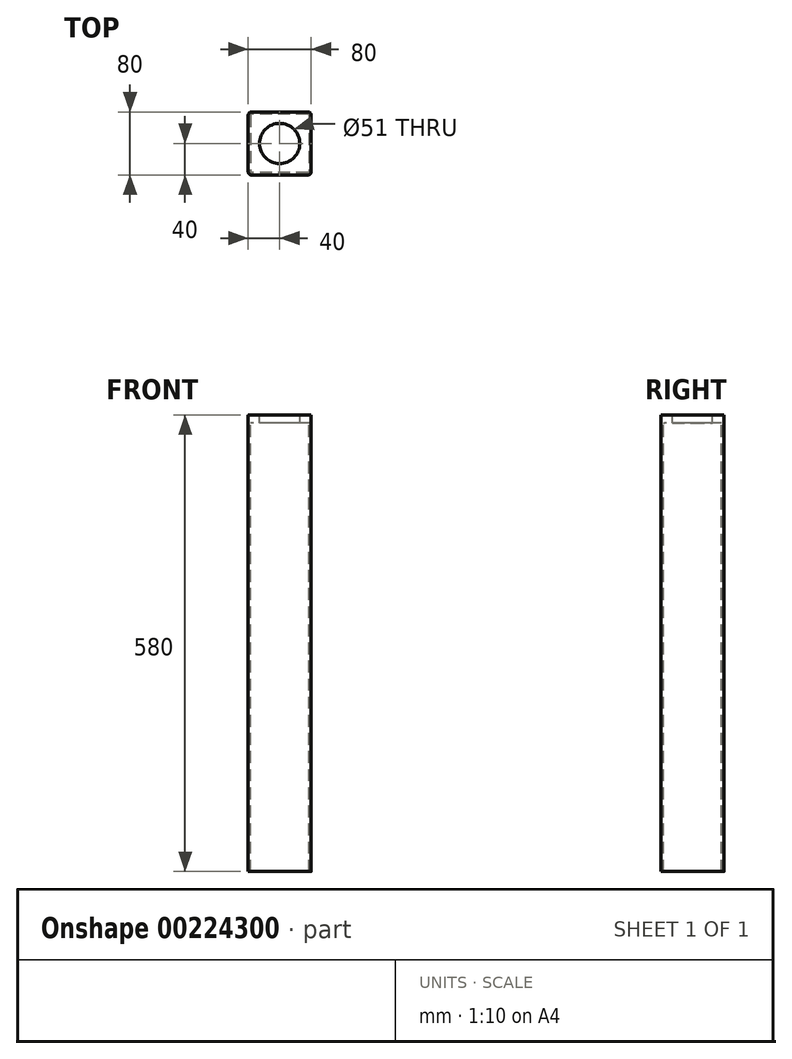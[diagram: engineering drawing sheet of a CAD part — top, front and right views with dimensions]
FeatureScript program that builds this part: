
annotation { "Feature Type Name" : "Feature", "Feature Type Description" : "" }
export const myFeature = defineFeature(function(context is Context, id is Id, definition is map)
    precondition{}
    {
        {
            var Q0;
            Q0=qCreatedBy(makeId("Top.planeOp"),FACE);
            var sketch = newSketch(context, id + "F0", { "sketchPlane" : qUnion([Q0])});
            skLineSegment(sketch, "E0.bottom", {"start": v(36, 40) * mm, "end": v(-36, 40) * mm});
            skLineSegment(sketch, "E0.top", {"start": v(36, -40) * mm, "end": v(-36, -40) * mm});
            skLineSegment(sketch, "E0.left", {"start": v(40, 36) * mm, "end": v(40, -36) * mm});
            skLineSegment(sketch, "E0.right", {"start": v(-40, 36) * mm, "end": v(-40, -36) * mm});
            skPoint(sketch, "E0.middle", {"position": v(0, 0) * mm});
            skPoint(sketch, "E1.visualSharp", {"position": v(-40, 40) * mm});
            skArc(sketch, "E1.filletArc", {"start": v(-36, 40) * mm, "mid": v(-38.83, 38.83) * mm, "end": v(-40, 36) * mm});
            skPoint(sketch, "E2.visualSharp", {"position": v(-40, -40) * mm});
            skArc(sketch, "E2.filletArc", {"start": v(-40, -36) * mm, "mid": v(-38.83, -38.83) * mm, "end": v(-36, -40) * mm});
            skPoint(sketch, "E3.visualSharp", {"position": v(40, -40) * mm});
            skArc(sketch, "E3.filletArc", {"start": v(36, -40) * mm, "mid": v(38.83, -38.83) * mm, "end": v(40, -36) * mm});
            skPoint(sketch, "E4.visualSharp", {"position": v(40, 40) * mm});
            skArc(sketch, "E4.filletArc", {"start": v(40, 36) * mm, "mid": v(38.83, 38.83) * mm, "end": v(36, 40) * mm});
            skArc(sketch, "E5.0", {"start": v(-36, 37) * mm, "mid": v(-36.7, 36.7) * mm, "end": v(-37, 36) * mm});
            skLineSegment(sketch, "E5.1", {"start": v(36, 37) * mm, "end": v(-36, 37) * mm});
            skLineSegment(sketch, "E5.2", {"start": v(-37, 36) * mm, "end": v(-37, -36) * mm});
            skArc(sketch, "E5.3", {"start": v(37, 36) * mm, "mid": v(36.7, 36.7) * mm, "end": v(36, 37) * mm});
            skArc(sketch, "E5.4", {"start": v(-37, -36) * mm, "mid": v(-36.7, -36.7) * mm, "end": v(-36, -37) * mm});
            skLineSegment(sketch, "E5.5", {"start": v(36, -37) * mm, "end": v(-36, -37) * mm});
            skArc(sketch, "E5.6", {"start": v(36, -37) * mm, "mid": v(36.7, -36.7) * mm, "end": v(37, -36) * mm});
            skLineSegment(sketch, "E5.7", {"start": v(37, 36) * mm, "end": v(37, -36) * mm});
            skCircle(sketch, "E6", {"center": v(0, 0) * mm, "radius": 25.5 * mm});
            skSolve(sketch);
        }
        {
            var Q0;
            Q0 = qSketchRegion(id + "F0", true);
            extrude(context, id + "F1", {"entities" : qUnion([Q0]), "oppositeDirection" : true, "depth" : 580 * mm});
        }
        {
            var Q0;
            Q0=makeQuery(id+"F0.imprint","IMPRINT",FACE,{"disambiguationData":[TD([[makeQuery(id+"F0.imprint","IMPRINT",EDGE,{"derivedFrom":sQuery(id+"F0.wireOp",EDGE,"E5.0")}),1.0]])]});
            extrude(context, id + "F2", {"entities" : qUnion([Q0]), "operationType" : NewBodyOperationType.ADD, "oppositeDirection" : true, "depth" : 10 * mm});
        }
    });
